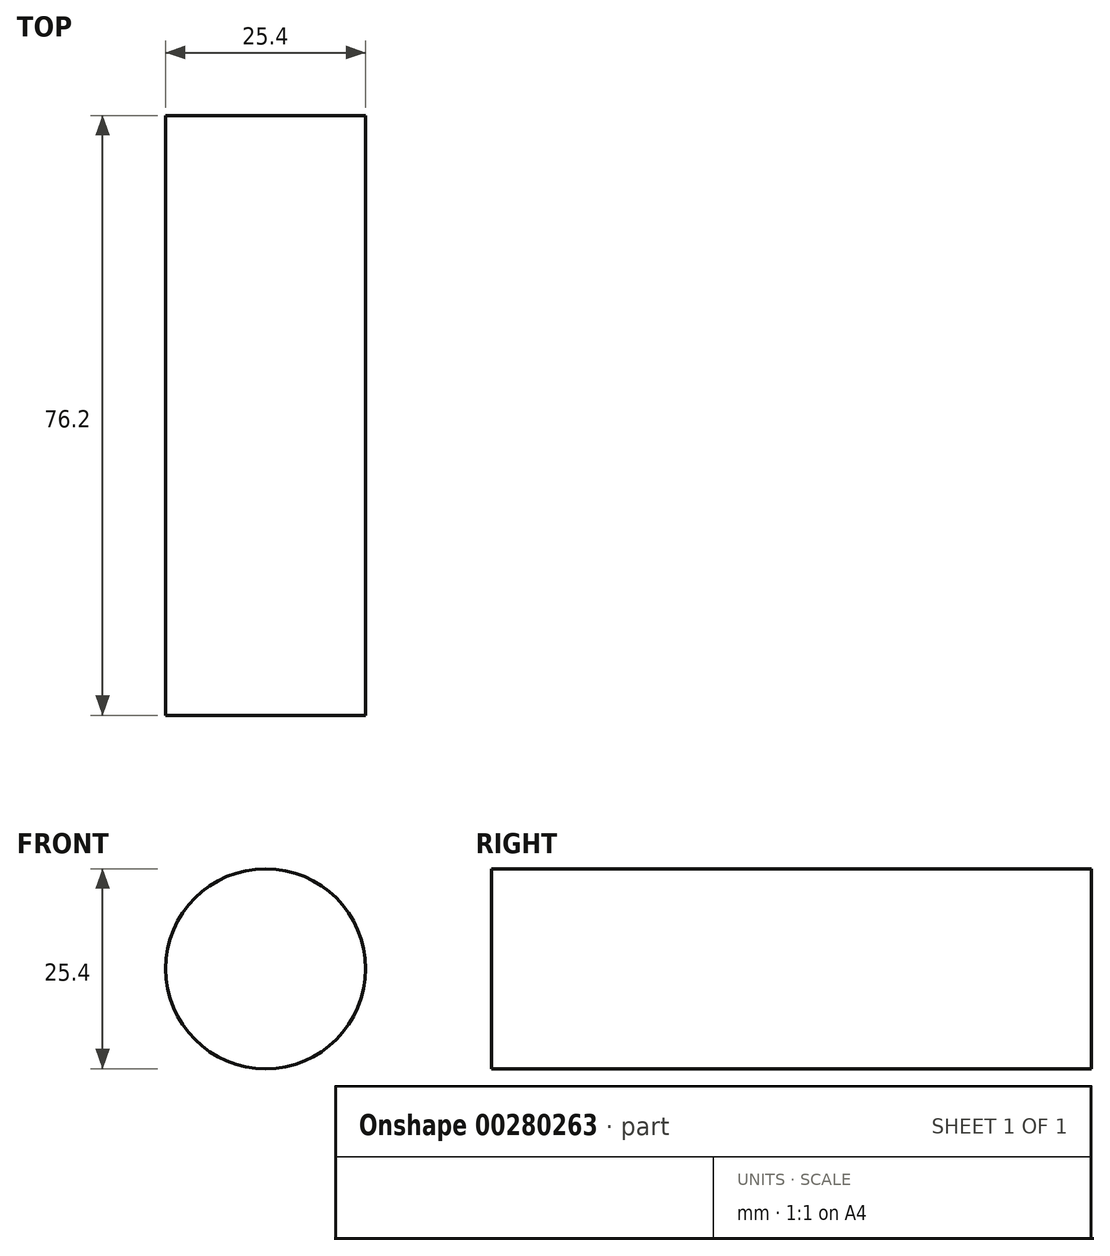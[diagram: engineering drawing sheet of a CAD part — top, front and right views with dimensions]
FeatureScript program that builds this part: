
annotation { "Feature Type Name" : "Feature", "Feature Type Description" : "" }
export const myFeature = defineFeature(function(context is Context, id is Id, definition is map)
    precondition{}
    {
        {
            var Q0;
            Q0=qCreatedBy(makeId("Front.planeOp"),FACE);
            var sketch = newSketch(context, id + "F0", { "sketchPlane" : qUnion([Q0])});
            skCircle(sketch, "E0", {"center": v(-49.08, 45.26) * mm, "radius": 12.7 * mm});
            skSolve(sketch);
        }
        {
            var Q0;
            Q0 = qSketchRegion(id + "F0", true);
            extrude(context, id + "F1", {"entities" : qUnion([Q0]), "depth" : 76.2 * mm});
        }
    });
